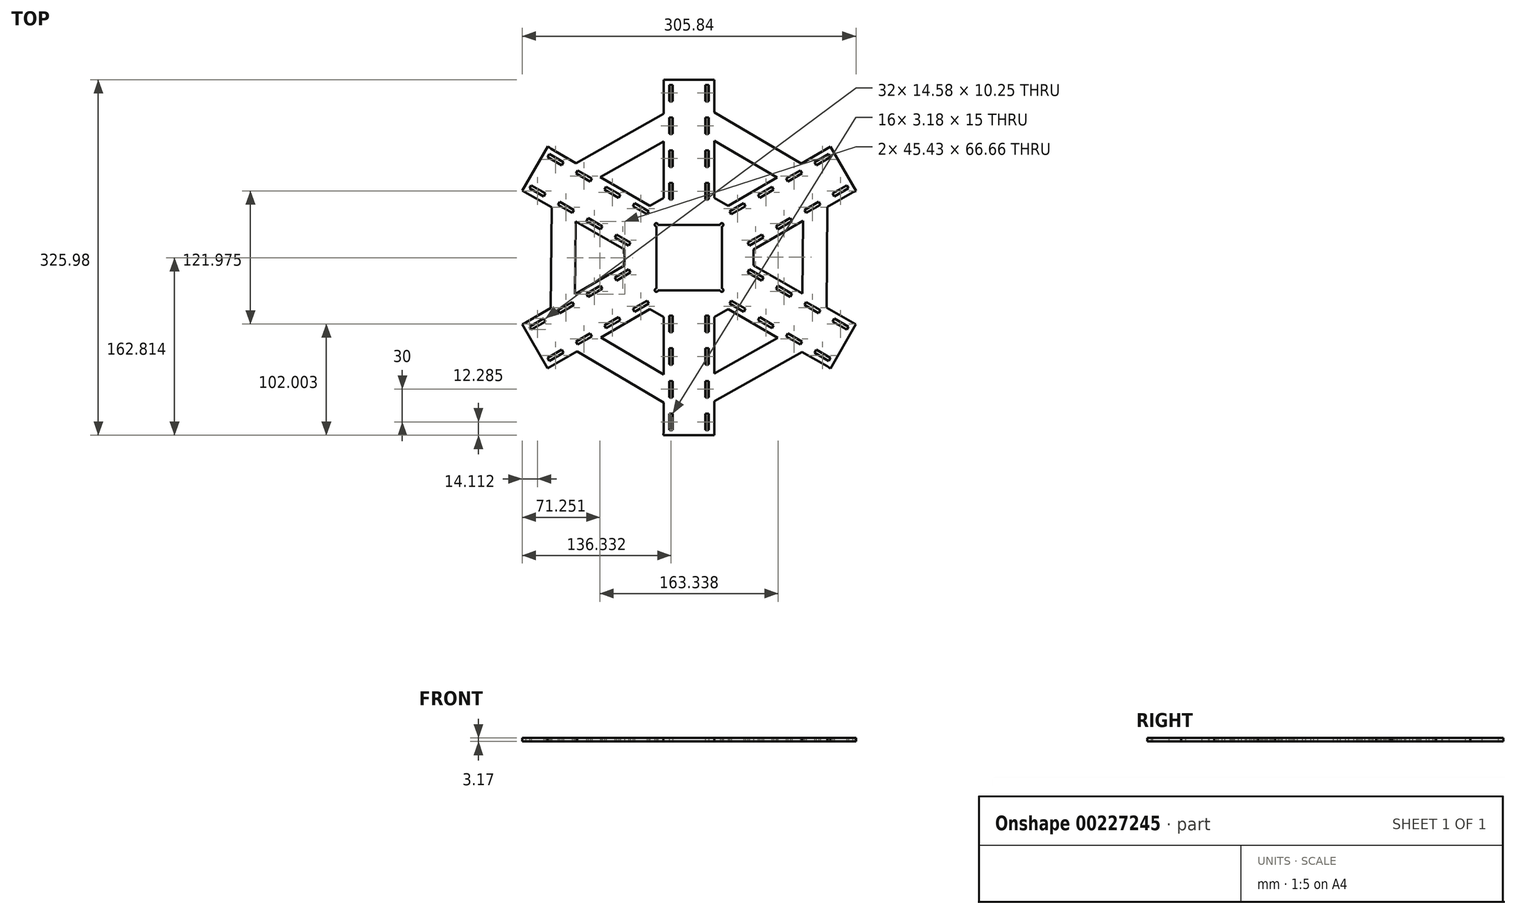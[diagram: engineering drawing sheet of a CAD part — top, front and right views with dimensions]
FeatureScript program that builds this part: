
annotation { "Feature Type Name" : "Feature", "Feature Type Description" : "" }
export const myFeature = defineFeature(function(context is Context, id is Id, definition is map)
    precondition{}
    {
        {
            var Q0;
            Q0=qCreatedBy(makeId("Top.planeOp"),FACE);
            var sketch = newSketch(context, id + "F0", { "sketchPlane" : qUnion([Q0])});
            skCircle(sketch, "E0.cCircle", {"center": v(0, 0) * mm, "radius": 173.2 * mm, "construction": true});
            skLineSegment(sketch, "E0.0", {"start": v(100, -173.2) * mm, "end": v(-100, -173.2) * mm});
            skLineSegment(sketch, "E0.1", {"start": v(-100, -173.2) * mm, "end": v(-200, 0) * mm});
            skLineSegment(sketch, "E0.2", {"start": v(-200, 0) * mm, "end": v(-100, 173.2) * mm});
            skLineSegment(sketch, "E0.3", {"start": v(-100, 173.2) * mm, "end": v(100, 173.2) * mm});
            skLineSegment(sketch, "E0.4", {"start": v(100, 173.2) * mm, "end": v(200, 0) * mm});
            skLineSegment(sketch, "E0.5", {"start": v(200, 0) * mm, "end": v(100, -173.2) * mm});
            skPoint(sketch, "E0.0.midPoint", {"position": v(0, -173.2) * mm});
            skLineSegment(sketch, "E1.bottom", {"start": v(-15, 143.2) * mm, "end": v(-18.18, 143.2) * mm});
            skLineSegment(sketch, "E1.top", {"start": v(-15, 158.2) * mm, "end": v(-18.18, 158.2) * mm});
            skLineSegment(sketch, "E1.left", {"start": v(-15, 143.2) * mm, "end": v(-15, 158.2) * mm});
            skLineSegment(sketch, "E1.right", {"start": v(-18.18, 143.2) * mm, "end": v(-18.18, 158.2) * mm});
            skPoint(sketch, "E1.middle", {"position": v(-16.59, 150.7) * mm});
            skPoint(sketch, "E2.0.1.0", {"position": v(-16.59, 120.7) * mm});
            skLineSegment(sketch, "E2.0.1.1", {"start": v(-18.18, 113.2) * mm, "end": v(-18.18, 128.2) * mm});
            skLineSegment(sketch, "E2.0.1.2", {"start": v(-15, 113.2) * mm, "end": v(-15, 128.2) * mm});
            skLineSegment(sketch, "E2.0.1.3", {"start": v(-15, 128.2) * mm, "end": v(-18.18, 128.2) * mm});
            skLineSegment(sketch, "E2.0.1.4", {"start": v(-15, 113.2) * mm, "end": v(-18.18, 113.2) * mm});
            skPoint(sketch, "E2.1.0.0", {"position": v(16.59, 150.7) * mm});
            skLineSegment(sketch, "E2.1.0.1", {"start": v(15, 143.2) * mm, "end": v(15, 158.2) * mm});
            skLineSegment(sketch, "E2.1.0.2", {"start": v(18.17, 143.2) * mm, "end": v(18.17, 158.2) * mm});
            skLineSegment(sketch, "E2.1.0.3", {"start": v(18.17, 158.2) * mm, "end": v(15, 158.2) * mm});
            skLineSegment(sketch, "E2.1.0.4", {"start": v(18.17, 143.2) * mm, "end": v(15, 143.2) * mm});
            skPoint(sketch, "E2.1.1.0", {"position": v(16.59, 120.7) * mm});
            skLineSegment(sketch, "E2.1.1.1", {"start": v(15, 113.2) * mm, "end": v(15, 128.2) * mm});
            skLineSegment(sketch, "E2.1.1.2", {"start": v(18.17, 113.2) * mm, "end": v(18.17, 128.2) * mm});
            skLineSegment(sketch, "E2.1.1.3", {"start": v(18.17, 128.2) * mm, "end": v(15, 128.2) * mm});
            skLineSegment(sketch, "E2.1.1.4", {"start": v(18.17, 113.2) * mm, "end": v(15, 113.2) * mm});
            skLineSegment(sketch, "E2.direction1", {"start": v(-18.18, 143.2) * mm, "end": v(15, 143.2) * mm, "construction": true});
            skLineSegment(sketch, "E2.direction2", {"start": v(-18.18, 143.2) * mm, "end": v(-18.18, 113.2) * mm, "construction": true});
            skLineSegment(sketch, "E3.1.0", {"start": v(-116.52, 84.6) * mm, "end": v(-129.5, 92.1) * mm});
            skLineSegment(sketch, "E3.1.1", {"start": v(-114.93, 87.34) * mm, "end": v(-127.92, 94.84) * mm});
            skPoint(sketch, "E3.1.2", {"position": v(-138.8, 60.99) * mm});
            skLineSegment(sketch, "E3.1.3", {"start": v(-133.1, 55.86) * mm, "end": v(-146.1, 63.36) * mm});
            skLineSegment(sketch, "E3.1.4", {"start": v(-131.52, 58.61) * mm, "end": v(-144.5, 66.11) * mm});
            skLineSegment(sketch, "E3.1.5", {"start": v(-107.13, 40.86) * mm, "end": v(-120.12, 48.36) * mm});
            skLineSegment(sketch, "E3.1.6", {"start": v(-133.1, 55.86) * mm, "end": v(-116.52, 84.6) * mm, "construction": true});
            skLineSegment(sketch, "E3.1.7", {"start": v(-105.54, 43.61) * mm, "end": v(-118.53, 51.11) * mm});
            skPoint(sketch, "E3.1.8", {"position": v(-122.22, 89.72) * mm});
            skLineSegment(sketch, "E3.1.9", {"start": v(-88.95, 72.34) * mm, "end": v(-101.94, 79.84) * mm});
            skLineSegment(sketch, "E3.1.10", {"start": v(-90.54, 69.6) * mm, "end": v(-103.53, 77.1) * mm});
            skLineSegment(sketch, "E3.1.11", {"start": v(-133.1, 55.86) * mm, "end": v(-107.13, 40.86) * mm, "construction": true});
            skPoint(sketch, "E3.1.12", {"position": v(-112.83, 45.99) * mm});
            skPoint(sketch, "E3.1.13", {"position": v(-96.24, 74.72) * mm});
            skLineSegment(sketch, "E3.1.14", {"start": v(-131.52, 58.61) * mm, "end": v(-133.1, 55.86) * mm});
            skLineSegment(sketch, "E3.1.15", {"start": v(-105.54, 43.61) * mm, "end": v(-107.13, 40.86) * mm});
            skLineSegment(sketch, "E3.1.16", {"start": v(-88.95, 72.34) * mm, "end": v(-90.54, 69.6) * mm});
            skLineSegment(sketch, "E3.1.17", {"start": v(-144.5, 66.11) * mm, "end": v(-146.1, 63.36) * mm});
            skLineSegment(sketch, "E3.1.18", {"start": v(-114.93, 87.34) * mm, "end": v(-116.52, 84.6) * mm});
            skLineSegment(sketch, "E3.1.19", {"start": v(-118.53, 51.11) * mm, "end": v(-120.12, 48.36) * mm});
            skLineSegment(sketch, "E3.1.20", {"start": v(-127.92, 94.84) * mm, "end": v(-129.5, 92.1) * mm});
            skLineSegment(sketch, "E3.1.21", {"start": v(-101.94, 79.84) * mm, "end": v(-103.53, 77.1) * mm});
            skLineSegment(sketch, "E3.2.0", {"start": v(-131.52, -58.61) * mm, "end": v(-144.5, -66.11) * mm});
            skLineSegment(sketch, "E3.2.1", {"start": v(-133.1, -55.86) * mm, "end": v(-146.1, -63.36) * mm});
            skPoint(sketch, "E3.2.2", {"position": v(-122.22, -89.72) * mm});
            skLineSegment(sketch, "E3.2.3", {"start": v(-114.93, -87.34) * mm, "end": v(-127.92, -94.84) * mm});
            skLineSegment(sketch, "E3.2.4", {"start": v(-116.52, -84.6) * mm, "end": v(-129.5, -92.1) * mm});
            skLineSegment(sketch, "E3.2.5", {"start": v(-88.95, -72.34) * mm, "end": v(-101.94, -79.84) * mm});
            skLineSegment(sketch, "E3.2.6", {"start": v(-114.93, -87.34) * mm, "end": v(-131.52, -58.61) * mm, "construction": true});
            skLineSegment(sketch, "E3.2.7", {"start": v(-90.54, -69.6) * mm, "end": v(-103.53, -77.1) * mm});
            skPoint(sketch, "E3.2.8", {"position": v(-138.8, -60.99) * mm});
            skLineSegment(sketch, "E3.2.9", {"start": v(-107.13, -40.86) * mm, "end": v(-120.12, -48.36) * mm});
            skLineSegment(sketch, "E3.2.10", {"start": v(-105.54, -43.61) * mm, "end": v(-118.53, -51.11) * mm});
            skLineSegment(sketch, "E3.2.11", {"start": v(-114.93, -87.34) * mm, "end": v(-88.95, -72.34) * mm, "construction": true});
            skPoint(sketch, "E3.2.12", {"position": v(-96.24, -74.72) * mm});
            skPoint(sketch, "E3.2.13", {"position": v(-112.83, -45.99) * mm});
            skLineSegment(sketch, "E3.2.14", {"start": v(-116.52, -84.6) * mm, "end": v(-114.93, -87.34) * mm});
            skLineSegment(sketch, "E3.2.15", {"start": v(-90.54, -69.6) * mm, "end": v(-88.95, -72.34) * mm});
            skLineSegment(sketch, "E3.2.16", {"start": v(-107.13, -40.86) * mm, "end": v(-105.54, -43.61) * mm});
            skLineSegment(sketch, "E3.2.17", {"start": v(-129.5, -92.1) * mm, "end": v(-127.92, -94.84) * mm});
            skLineSegment(sketch, "E3.2.18", {"start": v(-133.1, -55.86) * mm, "end": v(-131.52, -58.61) * mm});
            skLineSegment(sketch, "E3.2.19", {"start": v(-103.53, -77.1) * mm, "end": v(-101.94, -79.84) * mm});
            skLineSegment(sketch, "E3.2.20", {"start": v(-146.1, -63.36) * mm, "end": v(-144.5, -66.11) * mm});
            skLineSegment(sketch, "E3.2.21", {"start": v(-120.12, -48.36) * mm, "end": v(-118.53, -51.11) * mm});
            skLineSegment(sketch, "E3.3.0", {"start": v(-15, -143.2) * mm, "end": v(-15, -158.2) * mm});
            skLineSegment(sketch, "E3.3.1", {"start": v(-18.17, -143.2) * mm, "end": v(-18.17, -158.2) * mm});
            skPoint(sketch, "E3.3.2", {"position": v(16.59, -150.7) * mm});
            skLineSegment(sketch, "E3.3.3", {"start": v(18.18, -143.2) * mm, "end": v(18.18, -158.2) * mm});
            skLineSegment(sketch, "E3.3.4", {"start": v(15, -143.2) * mm, "end": v(15, -158.2) * mm});
            skLineSegment(sketch, "E3.3.5", {"start": v(18.18, -113.2) * mm, "end": v(18.18, -128.2) * mm});
            skLineSegment(sketch, "E3.3.6", {"start": v(18.17, -143.2) * mm, "end": v(-15, -143.2) * mm, "construction": true});
            skLineSegment(sketch, "E3.3.7", {"start": v(15, -113.2) * mm, "end": v(15, -128.2) * mm});
            skPoint(sketch, "E3.3.8", {"position": v(-16.59, -150.7) * mm});
            skLineSegment(sketch, "E3.3.9", {"start": v(-18.17, -113.2) * mm, "end": v(-18.17, -128.2) * mm});
            skLineSegment(sketch, "E3.3.10", {"start": v(-15, -113.2) * mm, "end": v(-15, -128.2) * mm});
            skLineSegment(sketch, "E3.3.11", {"start": v(18.18, -143.2) * mm, "end": v(18.18, -113.2) * mm, "construction": true});
            skPoint(sketch, "E3.3.12", {"position": v(16.59, -120.7) * mm});
            skPoint(sketch, "E3.3.13", {"position": v(-16.59, -120.7) * mm});
            skLineSegment(sketch, "E3.3.14", {"start": v(15, -143.2) * mm, "end": v(18.17, -143.2) * mm});
            skLineSegment(sketch, "E3.3.15", {"start": v(15, -113.2) * mm, "end": v(18.17, -113.2) * mm});
            skLineSegment(sketch, "E3.3.16", {"start": v(-18.18, -113.2) * mm, "end": v(-15, -113.2) * mm});
            skLineSegment(sketch, "E3.3.17", {"start": v(15, -158.2) * mm, "end": v(18.17, -158.2) * mm});
            skLineSegment(sketch, "E3.3.18", {"start": v(-18.18, -143.2) * mm, "end": v(-15, -143.2) * mm});
            skLineSegment(sketch, "E3.3.19", {"start": v(15, -128.2) * mm, "end": v(18.17, -128.2) * mm});
            skLineSegment(sketch, "E3.3.20", {"start": v(-18.18, -158.2) * mm, "end": v(-15, -158.2) * mm});
            skLineSegment(sketch, "E3.3.21", {"start": v(-18.18, -128.2) * mm, "end": v(-15, -128.2) * mm});
            skLineSegment(sketch, "E3.4.0", {"start": v(116.52, -84.6) * mm, "end": v(129.5, -92.1) * mm});
            skLineSegment(sketch, "E3.4.1", {"start": v(114.93, -87.34) * mm, "end": v(127.92, -94.84) * mm});
            skPoint(sketch, "E3.4.2", {"position": v(138.8, -60.99) * mm});
            skLineSegment(sketch, "E3.4.3", {"start": v(133.1, -55.86) * mm, "end": v(146.1, -63.36) * mm});
            skLineSegment(sketch, "E3.4.4", {"start": v(131.52, -58.61) * mm, "end": v(144.5, -66.11) * mm});
            skLineSegment(sketch, "E3.4.5", {"start": v(107.13, -40.86) * mm, "end": v(120.12, -48.36) * mm});
            skLineSegment(sketch, "E3.4.6", {"start": v(133.1, -55.86) * mm, "end": v(116.52, -84.6) * mm, "construction": true});
            skLineSegment(sketch, "E3.4.7", {"start": v(105.54, -43.61) * mm, "end": v(118.53, -51.11) * mm});
            skPoint(sketch, "E3.4.8", {"position": v(122.22, -89.72) * mm});
            skLineSegment(sketch, "E3.4.9", {"start": v(88.95, -72.34) * mm, "end": v(101.94, -79.84) * mm});
            skLineSegment(sketch, "E3.4.10", {"start": v(90.54, -69.6) * mm, "end": v(103.53, -77.1) * mm});
            skLineSegment(sketch, "E3.4.11", {"start": v(133.1, -55.86) * mm, "end": v(107.13, -40.86) * mm, "construction": true});
            skPoint(sketch, "E3.4.12", {"position": v(112.83, -45.99) * mm});
            skPoint(sketch, "E3.4.13", {"position": v(96.24, -74.72) * mm});
            skLineSegment(sketch, "E3.4.14", {"start": v(131.52, -58.61) * mm, "end": v(133.1, -55.86) * mm});
            skLineSegment(sketch, "E3.4.15", {"start": v(105.54, -43.61) * mm, "end": v(107.13, -40.86) * mm});
            skLineSegment(sketch, "E3.4.16", {"start": v(88.95, -72.34) * mm, "end": v(90.54, -69.6) * mm});
            skLineSegment(sketch, "E3.4.17", {"start": v(144.5, -66.11) * mm, "end": v(146.1, -63.36) * mm});
            skLineSegment(sketch, "E3.4.18", {"start": v(114.93, -87.34) * mm, "end": v(116.52, -84.6) * mm});
            skLineSegment(sketch, "E3.4.19", {"start": v(118.53, -51.11) * mm, "end": v(120.12, -48.36) * mm});
            skLineSegment(sketch, "E3.4.20", {"start": v(127.92, -94.84) * mm, "end": v(129.5, -92.1) * mm});
            skLineSegment(sketch, "E3.4.21", {"start": v(101.94, -79.84) * mm, "end": v(103.53, -77.1) * mm});
            skLineSegment(sketch, "E3.5.0", {"start": v(131.52, 58.61) * mm, "end": v(144.5, 66.11) * mm});
            skLineSegment(sketch, "E3.5.1", {"start": v(133.1, 55.86) * mm, "end": v(146.1, 63.36) * mm});
            skPoint(sketch, "E3.5.2", {"position": v(122.22, 89.72) * mm});
            skLineSegment(sketch, "E3.5.3", {"start": v(114.93, 87.34) * mm, "end": v(127.92, 94.84) * mm});
            skLineSegment(sketch, "E3.5.4", {"start": v(116.52, 84.6) * mm, "end": v(129.5, 92.1) * mm});
            skLineSegment(sketch, "E3.5.5", {"start": v(88.95, 72.34) * mm, "end": v(101.94, 79.84) * mm});
            skLineSegment(sketch, "E3.5.6", {"start": v(114.93, 87.34) * mm, "end": v(131.52, 58.61) * mm, "construction": true});
            skLineSegment(sketch, "E3.5.7", {"start": v(90.54, 69.6) * mm, "end": v(103.53, 77.1) * mm});
            skPoint(sketch, "E3.5.8", {"position": v(138.8, 60.99) * mm});
            skLineSegment(sketch, "E3.5.9", {"start": v(107.13, 40.86) * mm, "end": v(120.12, 48.36) * mm});
            skLineSegment(sketch, "E3.5.10", {"start": v(105.54, 43.61) * mm, "end": v(118.53, 51.11) * mm});
            skLineSegment(sketch, "E3.5.11", {"start": v(114.93, 87.34) * mm, "end": v(88.95, 72.34) * mm, "construction": true});
            skPoint(sketch, "E3.5.12", {"position": v(96.24, 74.72) * mm});
            skPoint(sketch, "E3.5.13", {"position": v(112.83, 45.99) * mm});
            skLineSegment(sketch, "E3.5.14", {"start": v(116.52, 84.6) * mm, "end": v(114.93, 87.34) * mm});
            skLineSegment(sketch, "E3.5.15", {"start": v(90.54, 69.6) * mm, "end": v(88.95, 72.34) * mm});
            skLineSegment(sketch, "E3.5.16", {"start": v(107.13, 40.86) * mm, "end": v(105.54, 43.61) * mm});
            skLineSegment(sketch, "E3.5.17", {"start": v(129.5, 92.1) * mm, "end": v(127.92, 94.84) * mm});
            skLineSegment(sketch, "E3.5.18", {"start": v(133.1, 55.86) * mm, "end": v(131.52, 58.61) * mm});
            skLineSegment(sketch, "E3.5.19", {"start": v(103.53, 77.1) * mm, "end": v(101.94, 79.84) * mm});
            skLineSegment(sketch, "E3.5.20", {"start": v(146.1, 63.36) * mm, "end": v(144.5, 66.11) * mm});
            skLineSegment(sketch, "E3.5.21", {"start": v(120.12, 48.36) * mm, "end": v(118.53, 51.11) * mm});
            skLineSegment(sketch, "E4.bottom", {"start": v(30, -30) * mm, "end": v(-30, -30) * mm});
            skLineSegment(sketch, "E4.top", {"start": v(30, 30) * mm, "end": v(-30, 30) * mm});
            skLineSegment(sketch, "E4.left", {"start": v(30, -30) * mm, "end": v(30, 30) * mm});
            skLineSegment(sketch, "E4.right", {"start": v(-30, -30) * mm, "end": v(-30, 30) * mm});
            skCircle(sketch, "E5", {"center": v(-30, 30) * mm, "radius": 1.5 * mm});
            skCircle(sketch, "E6.1.0", {"center": v(-30, -30) * mm, "radius": 1.5 * mm});
            skCircle(sketch, "E6.2.0", {"center": v(30, -30) * mm, "radius": 1.5 * mm});
            skCircle(sketch, "E6.3.0", {"center": v(30, 30) * mm, "radius": 1.5 * mm});
            skPoint(sketch, "E7.0.0.2", {"position": v(-16.59, 90.7) * mm});
            skLineSegment(sketch, "E7.1.0.2", {"start": v(-18.18, 83.2) * mm, "end": v(-18.18, 98.2) * mm});
            skLineSegment(sketch, "E7.4.0.2", {"start": v(-15, 83.2) * mm, "end": v(-15, 98.2) * mm});
            skLineSegment(sketch, "E7.7.0.2", {"start": v(-15, 98.2) * mm, "end": v(-18.18, 98.2) * mm});
            skLineSegment(sketch, "E7.10.0.2", {"start": v(-15, 83.2) * mm, "end": v(-18.18, 83.2) * mm});
            skPoint(sketch, "E7.0.1.2", {"position": v(16.59, 90.7) * mm});
            skLineSegment(sketch, "E7.1.1.2", {"start": v(15, 83.2) * mm, "end": v(15, 98.2) * mm});
            skLineSegment(sketch, "E7.4.1.2", {"start": v(18.17, 83.2) * mm, "end": v(18.17, 98.2) * mm});
            skLineSegment(sketch, "E7.7.1.2", {"start": v(18.17, 98.2) * mm, "end": v(15, 98.2) * mm});
            skLineSegment(sketch, "E7.10.1.2", {"start": v(18.17, 83.2) * mm, "end": v(15, 83.2) * mm});
            skPoint(sketch, "E8.0.0.3", {"position": v(-16.59, 60.7) * mm});
            skLineSegment(sketch, "E8.1.0.3", {"start": v(-18.18, 53.2) * mm, "end": v(-18.18, 68.2) * mm});
            skLineSegment(sketch, "E8.4.0.3", {"start": v(-15, 53.2) * mm, "end": v(-15, 68.2) * mm});
            skLineSegment(sketch, "E8.7.0.3", {"start": v(-15, 68.2) * mm, "end": v(-18.18, 68.2) * mm});
            skLineSegment(sketch, "E8.10.0.3", {"start": v(-15, 53.2) * mm, "end": v(-18.18, 53.2) * mm});
            skPoint(sketch, "E8.0.1.3", {"position": v(16.59, 60.7) * mm});
            skLineSegment(sketch, "E8.1.1.3", {"start": v(15, 53.2) * mm, "end": v(15, 68.2) * mm});
            skLineSegment(sketch, "E8.4.1.3", {"start": v(18.17, 53.2) * mm, "end": v(18.17, 68.2) * mm});
            skLineSegment(sketch, "E8.7.1.3", {"start": v(18.17, 68.2) * mm, "end": v(15, 68.2) * mm});
            skLineSegment(sketch, "E8.10.1.3", {"start": v(18.18, 53.2) * mm, "end": v(15, 53.2) * mm});
            skPoint(sketch, "E9.1.0", {"position": v(-60.87, 15.99) * mm});
            skPoint(sketch, "E9.1.1", {"position": v(-86.85, 30.99) * mm});
            skPoint(sketch, "E9.1.2", {"position": v(-44.28, 44.72) * mm});
            skPoint(sketch, "E9.1.3", {"position": v(-70.26, 59.72) * mm});
            skLineSegment(sketch, "E9.1.4", {"start": v(-55.16, 10.86) * mm, "end": v(-68.15, 18.36) * mm});
            skLineSegment(sketch, "E9.1.5", {"start": v(-36.99, 42.34) * mm, "end": v(-49.98, 49.84) * mm});
            skLineSegment(sketch, "E9.1.6", {"start": v(-79.56, 28.61) * mm, "end": v(-92.55, 36.11) * mm});
            skLineSegment(sketch, "E9.1.7", {"start": v(-64.56, 54.6) * mm, "end": v(-77.55, 62.1) * mm});
            skLineSegment(sketch, "E9.1.8", {"start": v(-62.97, 57.34) * mm, "end": v(-75.96, 64.84) * mm});
            skLineSegment(sketch, "E9.1.9", {"start": v(-53.58, 13.61) * mm, "end": v(-66.57, 21.11) * mm});
            skLineSegment(sketch, "E9.1.10", {"start": v(-38.58, 39.6) * mm, "end": v(-51.57, 47.1) * mm});
            skLineSegment(sketch, "E9.1.11", {"start": v(-81.15, 25.86) * mm, "end": v(-94.14, 33.36) * mm});
            skLineSegment(sketch, "E9.1.12", {"start": v(-79.56, 28.61) * mm, "end": v(-81.15, 25.86) * mm});
            skLineSegment(sketch, "E9.1.13", {"start": v(-62.97, 57.34) * mm, "end": v(-64.56, 54.6) * mm});
            skLineSegment(sketch, "E9.1.14", {"start": v(-49.98, 49.84) * mm, "end": v(-51.57, 47.1) * mm});
            skLineSegment(sketch, "E9.1.15", {"start": v(-36.99, 42.34) * mm, "end": v(-38.58, 39.6) * mm});
            skLineSegment(sketch, "E9.1.16", {"start": v(-75.96, 64.84) * mm, "end": v(-77.55, 62.1) * mm});
            skLineSegment(sketch, "E9.1.17", {"start": v(-92.55, 36.11) * mm, "end": v(-94.14, 33.36) * mm});
            skLineSegment(sketch, "E9.1.18", {"start": v(-53.58, 13.61) * mm, "end": v(-55.16, 10.86) * mm});
            skLineSegment(sketch, "E9.1.19", {"start": v(-66.57, 21.11) * mm, "end": v(-68.15, 18.36) * mm});
            skPoint(sketch, "E9.2.0", {"position": v(-44.28, -44.72) * mm});
            skPoint(sketch, "E9.2.1", {"position": v(-70.26, -59.72) * mm});
            skPoint(sketch, "E9.2.2", {"position": v(-60.87, -15.99) * mm});
            skPoint(sketch, "E9.2.3", {"position": v(-86.85, -30.99) * mm});
            skLineSegment(sketch, "E9.2.4", {"start": v(-36.99, -42.34) * mm, "end": v(-49.98, -49.84) * mm});
            skLineSegment(sketch, "E9.2.5", {"start": v(-55.16, -10.86) * mm, "end": v(-68.15, -18.36) * mm});
            skLineSegment(sketch, "E9.2.6", {"start": v(-64.56, -54.6) * mm, "end": v(-77.55, -62.1) * mm});
            skLineSegment(sketch, "E9.2.7", {"start": v(-79.56, -28.61) * mm, "end": v(-92.55, -36.11) * mm});
            skLineSegment(sketch, "E9.2.8", {"start": v(-81.15, -25.86) * mm, "end": v(-94.14, -33.36) * mm});
            skLineSegment(sketch, "E9.2.9", {"start": v(-38.58, -39.6) * mm, "end": v(-51.57, -47.1) * mm});
            skLineSegment(sketch, "E9.2.10", {"start": v(-53.58, -13.61) * mm, "end": v(-66.57, -21.11) * mm});
            skLineSegment(sketch, "E9.2.11", {"start": v(-62.97, -57.34) * mm, "end": v(-75.96, -64.84) * mm});
            skLineSegment(sketch, "E9.2.12", {"start": v(-64.56, -54.6) * mm, "end": v(-62.97, -57.34) * mm});
            skLineSegment(sketch, "E9.2.13", {"start": v(-81.15, -25.86) * mm, "end": v(-79.56, -28.61) * mm});
            skLineSegment(sketch, "E9.2.14", {"start": v(-68.15, -18.36) * mm, "end": v(-66.57, -21.11) * mm});
            skLineSegment(sketch, "E9.2.15", {"start": v(-55.16, -10.86) * mm, "end": v(-53.58, -13.61) * mm});
            skLineSegment(sketch, "E9.2.16", {"start": v(-94.14, -33.36) * mm, "end": v(-92.55, -36.11) * mm});
            skLineSegment(sketch, "E9.2.17", {"start": v(-77.55, -62.1) * mm, "end": v(-75.96, -64.84) * mm});
            skLineSegment(sketch, "E9.2.18", {"start": v(-38.58, -39.6) * mm, "end": v(-36.99, -42.34) * mm});
            skLineSegment(sketch, "E9.2.19", {"start": v(-51.57, -47.1) * mm, "end": v(-49.98, -49.84) * mm});
            skPoint(sketch, "E9.3.0", {"position": v(16.59, -60.7) * mm});
            skPoint(sketch, "E9.3.1", {"position": v(16.59, -90.7) * mm});
            skPoint(sketch, "E9.3.2", {"position": v(-16.59, -60.7) * mm});
            skPoint(sketch, "E9.3.3", {"position": v(-16.59, -90.7) * mm});
            skLineSegment(sketch, "E9.3.4", {"start": v(18.18, -53.2) * mm, "end": v(18.18, -68.2) * mm});
            skLineSegment(sketch, "E9.3.5", {"start": v(-18.17, -53.2) * mm, "end": v(-18.17, -68.2) * mm});
            skLineSegment(sketch, "E9.3.6", {"start": v(15, -83.2) * mm, "end": v(15, -98.2) * mm});
            skLineSegment(sketch, "E9.3.7", {"start": v(-15, -83.2) * mm, "end": v(-15, -98.2) * mm});
            skLineSegment(sketch, "E9.3.8", {"start": v(-18.17, -83.2) * mm, "end": v(-18.17, -98.2) * mm});
            skLineSegment(sketch, "E9.3.9", {"start": v(15, -53.2) * mm, "end": v(15, -68.2) * mm});
            skLineSegment(sketch, "E9.3.10", {"start": v(-15, -53.2) * mm, "end": v(-15, -68.2) * mm});
            skLineSegment(sketch, "E9.3.11", {"start": v(18.18, -83.2) * mm, "end": v(18.18, -98.2) * mm});
            skLineSegment(sketch, "E9.3.12", {"start": v(15, -83.2) * mm, "end": v(18.17, -83.2) * mm});
            skLineSegment(sketch, "E9.3.13", {"start": v(-18.18, -83.2) * mm, "end": v(-15, -83.2) * mm});
            skLineSegment(sketch, "E9.3.14", {"start": v(-18.18, -68.2) * mm, "end": v(-15, -68.2) * mm});
            skLineSegment(sketch, "E9.3.15", {"start": v(-18.18, -53.2) * mm, "end": v(-15, -53.2) * mm});
            skLineSegment(sketch, "E9.3.16", {"start": v(-18.18, -98.2) * mm, "end": v(-15, -98.2) * mm});
            skLineSegment(sketch, "E9.3.17", {"start": v(15, -98.2) * mm, "end": v(18.17, -98.2) * mm});
            skLineSegment(sketch, "E9.3.18", {"start": v(15, -53.2) * mm, "end": v(18.17, -53.2) * mm});
            skLineSegment(sketch, "E9.3.19", {"start": v(15, -68.2) * mm, "end": v(18.17, -68.2) * mm});
            skPoint(sketch, "E9.4.0", {"position": v(60.87, -15.99) * mm});
            skPoint(sketch, "E9.4.1", {"position": v(86.85, -30.99) * mm});
            skPoint(sketch, "E9.4.2", {"position": v(44.28, -44.72) * mm});
            skPoint(sketch, "E9.4.3", {"position": v(70.26, -59.72) * mm});
            skLineSegment(sketch, "E9.4.4", {"start": v(55.16, -10.86) * mm, "end": v(68.15, -18.36) * mm});
            skLineSegment(sketch, "E9.4.5", {"start": v(36.99, -42.34) * mm, "end": v(49.98, -49.84) * mm});
            skLineSegment(sketch, "E9.4.6", {"start": v(79.56, -28.61) * mm, "end": v(92.55, -36.11) * mm});
            skLineSegment(sketch, "E9.4.7", {"start": v(64.56, -54.6) * mm, "end": v(77.55, -62.1) * mm});
            skLineSegment(sketch, "E9.4.8", {"start": v(62.97, -57.34) * mm, "end": v(75.96, -64.84) * mm});
            skLineSegment(sketch, "E9.4.9", {"start": v(53.58, -13.61) * mm, "end": v(66.57, -21.11) * mm});
            skLineSegment(sketch, "E9.4.10", {"start": v(38.58, -39.6) * mm, "end": v(51.57, -47.1) * mm});
            skLineSegment(sketch, "E9.4.11", {"start": v(81.15, -25.86) * mm, "end": v(94.14, -33.36) * mm});
            skLineSegment(sketch, "E9.4.12", {"start": v(79.56, -28.61) * mm, "end": v(81.15, -25.86) * mm});
            skLineSegment(sketch, "E9.4.13", {"start": v(62.97, -57.34) * mm, "end": v(64.56, -54.6) * mm});
            skLineSegment(sketch, "E9.4.14", {"start": v(49.98, -49.84) * mm, "end": v(51.57, -47.1) * mm});
            skLineSegment(sketch, "E9.4.15", {"start": v(36.99, -42.34) * mm, "end": v(38.58, -39.6) * mm});
            skLineSegment(sketch, "E9.4.16", {"start": v(75.96, -64.84) * mm, "end": v(77.55, -62.1) * mm});
            skLineSegment(sketch, "E9.4.17", {"start": v(92.55, -36.11) * mm, "end": v(94.14, -33.36) * mm});
            skLineSegment(sketch, "E9.4.18", {"start": v(53.58, -13.61) * mm, "end": v(55.16, -10.86) * mm});
            skLineSegment(sketch, "E9.4.19", {"start": v(66.57, -21.11) * mm, "end": v(68.15, -18.36) * mm});
            skPoint(sketch, "E9.5.0", {"position": v(44.28, 44.72) * mm});
            skPoint(sketch, "E9.5.1", {"position": v(70.26, 59.72) * mm});
            skPoint(sketch, "E9.5.2", {"position": v(60.87, 15.99) * mm});
            skPoint(sketch, "E9.5.3", {"position": v(86.85, 30.99) * mm});
            skLineSegment(sketch, "E9.5.4", {"start": v(36.99, 42.34) * mm, "end": v(49.98, 49.84) * mm});
            skLineSegment(sketch, "E9.5.5", {"start": v(55.16, 10.86) * mm, "end": v(68.15, 18.36) * mm});
            skLineSegment(sketch, "E9.5.6", {"start": v(64.56, 54.6) * mm, "end": v(77.55, 62.1) * mm});
            skLineSegment(sketch, "E9.5.7", {"start": v(79.56, 28.61) * mm, "end": v(92.55, 36.11) * mm});
            skLineSegment(sketch, "E9.5.8", {"start": v(81.15, 25.86) * mm, "end": v(94.14, 33.36) * mm});
            skLineSegment(sketch, "E9.5.9", {"start": v(38.58, 39.6) * mm, "end": v(51.57, 47.1) * mm});
            skLineSegment(sketch, "E9.5.10", {"start": v(53.58, 13.61) * mm, "end": v(66.57, 21.11) * mm});
            skLineSegment(sketch, "E9.5.11", {"start": v(62.97, 57.34) * mm, "end": v(75.96, 64.84) * mm});
            skLineSegment(sketch, "E9.5.12", {"start": v(64.56, 54.6) * mm, "end": v(62.97, 57.34) * mm});
            skLineSegment(sketch, "E9.5.13", {"start": v(81.15, 25.86) * mm, "end": v(79.56, 28.61) * mm});
            skLineSegment(sketch, "E9.5.14", {"start": v(68.15, 18.36) * mm, "end": v(66.57, 21.11) * mm});
            skLineSegment(sketch, "E9.5.15", {"start": v(55.16, 10.86) * mm, "end": v(53.58, 13.61) * mm});
            skLineSegment(sketch, "E9.5.16", {"start": v(94.14, 33.36) * mm, "end": v(92.55, 36.11) * mm});
            skLineSegment(sketch, "E9.5.17", {"start": v(77.55, 62.1) * mm, "end": v(75.96, 64.84) * mm});
            skLineSegment(sketch, "E9.5.18", {"start": v(38.58, 39.6) * mm, "end": v(36.99, 42.34) * mm});
            skLineSegment(sketch, "E9.5.19", {"start": v(51.57, 47.1) * mm, "end": v(49.98, 49.84) * mm});
            skLineSegment(sketch, "E10", {"start": v(-126.5, 99.8) * mm, "end": v(-35.78, 47.42) * mm});
            skLineSegment(sketch, "E11", {"start": v(-35.78, 47.42) * mm, "end": v(-23.17, 54.7) * mm});
            skLineSegment(sketch, "E12", {"start": v(-23.18, 54.7) * mm, "end": v(-23.18, 158.2) * mm});
            skLineSegment(sketch, "E13", {"start": v(-23.17, 158.2) * mm, "end": v(-126.5, 99.8) * mm});
            skLineSegment(sketch, "E14.1.0", {"start": v(-148.6, 59.03) * mm, "end": v(-149.68, -59.66) * mm});
            skLineSegment(sketch, "E14.1.1", {"start": v(-58.95, 7.28) * mm, "end": v(-148.6, 59.03) * mm});
            skLineSegment(sketch, "E14.1.2", {"start": v(-149.68, -59.66) * mm, "end": v(-58.95, -7.28) * mm});
            skLineSegment(sketch, "E14.1.3", {"start": v(-58.95, -7.28) * mm, "end": v(-58.95, 7.28) * mm});
            skLineSegment(sketch, "E14.2.0", {"start": v(-125.42, -99.17) * mm, "end": v(-23.18, -159.46) * mm});
            skLineSegment(sketch, "E14.2.1", {"start": v(-35.78, -47.42) * mm, "end": v(-125.42, -99.17) * mm});
            skLineSegment(sketch, "E14.2.2", {"start": v(-23.18, -159.46) * mm, "end": v(-23.18, -54.7) * mm});
            skLineSegment(sketch, "E14.2.3", {"start": v(-23.18, -54.7) * mm, "end": v(-35.78, -47.42) * mm});
            skLineSegment(sketch, "E14.3.0", {"start": v(23.17, -158.2) * mm, "end": v(126.5, -99.8) * mm});
            skLineSegment(sketch, "E14.3.1", {"start": v(23.17, -54.7) * mm, "end": v(23.17, -158.2) * mm});
            skLineSegment(sketch, "E14.3.2", {"start": v(126.5, -99.8) * mm, "end": v(35.78, -47.42) * mm});
            skLineSegment(sketch, "E14.3.3", {"start": v(35.78, -47.42) * mm, "end": v(23.17, -54.7) * mm});
            skLineSegment(sketch, "E14.4.0", {"start": v(148.6, -59.03) * mm, "end": v(149.68, 59.66) * mm});
            skLineSegment(sketch, "E14.4.1", {"start": v(58.95, -7.28) * mm, "end": v(148.6, -59.03) * mm});
            skLineSegment(sketch, "E14.4.2", {"start": v(149.68, 59.66) * mm, "end": v(58.95, 7.28) * mm});
            skLineSegment(sketch, "E14.4.3", {"start": v(58.95, 7.28) * mm, "end": v(58.95, -7.28) * mm});
            skLineSegment(sketch, "E14.5.0", {"start": v(125.42, 99.17) * mm, "end": v(23.17, 159.46) * mm});
            skLineSegment(sketch, "E14.5.1", {"start": v(35.78, 47.42) * mm, "end": v(125.42, 99.17) * mm});
            skLineSegment(sketch, "E14.5.2", {"start": v(23.17, 159.46) * mm, "end": v(23.18, 54.7) * mm});
            skLineSegment(sketch, "E14.5.3", {"start": v(23.18, 54.7) * mm, "end": v(35.78, 47.42) * mm});
            skLineSegment(sketch, "E15", {"start": v(-103.5, 86.51) * mm, "end": v(-23.18, 131.91) * mm});
            skLineSegment(sketch, "E16", {"start": v(-23.18, 131.91) * mm, "end": v(-23.18, 106.45) * mm});
            skLineSegment(sketch, "E17", {"start": v(-23.18, 106.45) * mm, "end": v(-81.21, 73.65) * mm});
            skLineSegment(sketch, "E18.1.0", {"start": v(-126.67, -46.37) * mm, "end": v(-125.83, 45.89) * mm});
            skLineSegment(sketch, "E18.1.1", {"start": v(-103.77, 33.15) * mm, "end": v(-104.39, -33.5) * mm});
            skLineSegment(sketch, "E18.2.0", {"start": v(-23.18, -132.89) * mm, "end": v(-102.65, -86.03) * mm});
            skLineSegment(sketch, "E18.2.1", {"start": v(-80.6, -73.3) * mm, "end": v(-23.17, -107.15) * mm});
            skLineSegment(sketch, "E19.1.3.0", {"start": v(103.5, -86.51) * mm, "end": v(23.17, -131.91) * mm});
            skLineSegment(sketch, "E19.3.3.0", {"start": v(23.17, -106.45) * mm, "end": v(81.21, -73.65) * mm});
            skLineSegment(sketch, "E19.1.4.0", {"start": v(126.67, 46.37) * mm, "end": v(125.83, -45.89) * mm});
            skLineSegment(sketch, "E19.3.4.0", {"start": v(103.77, -33.15) * mm, "end": v(104.39, 33.5) * mm});
            skLineSegment(sketch, "E19.1.5.0", {"start": v(23.17, 132.89) * mm, "end": v(102.65, 86.03) * mm});
            skLineSegment(sketch, "E19.3.5.0", {"start": v(80.6, 73.3) * mm, "end": v(23.17, 107.15) * mm});
            skLineSegment(sketch, "E20", {"start": v(-148.6, 59.03) * mm, "end": v(-152.74, 61.42) * mm});
            skLineSegment(sketch, "E21", {"start": v(-152.74, 61.42) * mm, "end": v(-129.39, 101.87) * mm});
            skLineSegment(sketch, "E22", {"start": v(-129.39, 101.87) * mm, "end": v(-126.5, 99.8) * mm});
            skLineSegment(sketch, "E23.1.0", {"start": v(-129.57, -101.56) * mm, "end": v(-152.92, -61.12) * mm});
            skLineSegment(sketch, "E23.1.1", {"start": v(-152.92, -61.12) * mm, "end": v(-149.68, -59.66) * mm});
            skLineSegment(sketch, "E23.1.2", {"start": v(-125.42, -99.17) * mm, "end": v(-129.57, -101.56) * mm});
            skLineSegment(sketch, "E23.2.0", {"start": v(23.17, -162.99) * mm, "end": v(-23.53, -162.99) * mm});
            skLineSegment(sketch, "E23.2.1", {"start": v(-23.53, -162.99) * mm, "end": v(-23.18, -159.46) * mm});
            skLineSegment(sketch, "E23.2.2", {"start": v(23.17, -158.2) * mm, "end": v(23.17, -162.99) * mm});
            skLineSegment(sketch, "E23.3.0", {"start": v(152.74, -61.42) * mm, "end": v(129.39, -101.87) * mm});
            skLineSegment(sketch, "E23.3.1", {"start": v(129.39, -101.87) * mm, "end": v(126.5, -99.8) * mm});
            skLineSegment(sketch, "E23.3.2", {"start": v(148.6, -59.03) * mm, "end": v(152.74, -61.42) * mm});
            skLineSegment(sketch, "E23.4.0", {"start": v(129.57, 101.56) * mm, "end": v(152.92, 61.12) * mm});
            skLineSegment(sketch, "E23.4.1", {"start": v(152.92, 61.12) * mm, "end": v(149.68, 59.66) * mm});
            skLineSegment(sketch, "E23.4.2", {"start": v(125.42, 99.17) * mm, "end": v(129.57, 101.56) * mm});
            skLineSegment(sketch, "E23.5.2", {"start": v(-23.18, 158.2) * mm, "end": v(-23.18, 162.99) * mm});
            skLineSegment(sketch, "E24", {"start": v(23.17, 159.46) * mm, "end": v(23.17, 162.99) * mm});
            skLineSegment(sketch, "E25", {"start": v(23.17, 162.99) * mm, "end": v(-23.18, 162.99) * mm});
            skSolve(sketch);
        }
        {
            var Q0;
            {var subQ0=sQuery(id+"F0.wireOp",EDGE,"E15");Q0=makeQuery(id+"F0.imprint","IMPRINT",FACE,{"disambiguationData":[TD([[makeQuery(id+"F0.imprint","IMPRINT",EDGE,{"derivedFrom":subQ0}),-1.0]])]});}
            var Q1;
            {var subQ0=sQuery(id+"F0.wireOp",EDGE,"E18.1.0");Q1=makeQuery(id+"F0.imprint","IMPRINT",FACE,{"disambiguationData":[TD([[makeQuery(id+"F0.imprint","IMPRINT",EDGE,{"derivedFrom":subQ0}),-1.0]])]});}
            var Q2;
            {var subQ0=sQuery(id+"F0.wireOp",EDGE,"E18.2.0");Q2=makeQuery(id+"F0.imprint","IMPRINT",FACE,{"disambiguationData":[TD([[makeQuery(id+"F0.imprint","IMPRINT",EDGE,{"derivedFrom":subQ0}),-1.0]])]});}
            var Q3;
            {var subQ0=sQuery(id+"F0.wireOp",EDGE,"E19.1.3.0");Q3=makeQuery(id+"F0.imprint","IMPRINT",FACE,{"disambiguationData":[TD([[makeQuery(id+"F0.imprint","IMPRINT",EDGE,{"derivedFrom":subQ0}),-1.0]])]});}
            var Q4;
            {var subQ0=sQuery(id+"F0.wireOp",EDGE,"E19.1.4.0");Q4=makeQuery(id+"F0.imprint","IMPRINT",FACE,{"disambiguationData":[TD([[makeQuery(id+"F0.imprint","IMPRINT",EDGE,{"derivedFrom":subQ0}),-1.0]])]});}
            var Q5;
            {var subQ0=sQuery(id+"F0.wireOp",EDGE,"E19.1.5.0");Q5=makeQuery(id+"F0.imprint","IMPRINT",FACE,{"disambiguationData":[TD([[makeQuery(id+"F0.imprint","IMPRINT",EDGE,{"derivedFrom":subQ0}),-1.0]])]});}
            var Q6;
            Q6=makeQuery(id+"F0.imprint","IMPRINT",FACE,{"disambiguationData":[TD([[makeQuery(id+"F0.imprint","IMPRINT",EDGE,{"derivedFrom":sQuery(id+"F0.wireOp",EDGE,"E1.bottom")}),1.0]])]});
            extrude(context, id + "F1", {"entities" : qUnion([Q0, Q1, Q2, Q3, Q4, Q5, Q6]), "depth" : 3.17 * mm});
        }
    });
